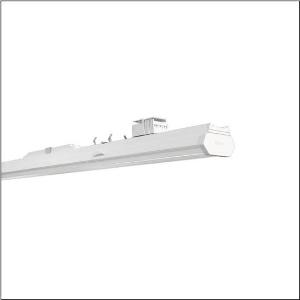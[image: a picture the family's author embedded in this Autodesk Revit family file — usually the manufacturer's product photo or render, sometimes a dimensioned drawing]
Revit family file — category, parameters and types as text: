
# Revit family: licross_r__21_protected_ho_52td12dn4e5m3c_ce33
name_source: partatom
category: Lighting Fixtures
units: mm (PartAtom-declared; Revit-internal decimal feet)

## family parameters
Cut with Voids When Loaded = No
Host = Face
Light Source = No
Part Type = Normal
Room Calculation Point = No
Round Connector Dimension = Use Diameter
Shared = No

## types (1)
- --- (1 x LED, 910 lm, 7.6 W, 4000K)
    Apparent Load = 8 VA
    CIE Flux Codes = 70 91 97 98 100
    Color Rendering = 80
    Color Temperature = 4000K
    Default Elevation = 1800 mm
    Description = Licross® 21 Protected HO, luminaire insert, of sheet steel, galvanised, coil coated, white, length: 1.500mm, width: 90mm, height: 103mm, LED rated luminous flux: 14.690lm, light colour: 840, SDCM (Standard Deviation of Colour Matching)MacAdam ≤ 3 SDCM (initial), control gear: DALI 2 (for two DALI lines), with plug, 6-pole, with phase selection, for trunking rail, 14-core, mains connection: 220..240V, AC, 50/60Hz, rated input power: 89W, for trunking rail, 14-core, internal wiring halogen-free, for emergency light function, converter,control gear: single battery element, battery: LiFePO4, 9Ah, primary light control with lens, of plastic, primary optical cover: cover, of PMMA, light emission: direct distribution, primary light characteristic: symmetric, protection rating (complete): IP54, insulation class (complete): insulation class I (protective earthing), certification: CE, UKCA, protection symbol: D if used in an environment with non-conductive dust loads with corresponding accessories, impact resistance: IK06, permissible ambient temperature for indoor applications: +5..+30°C, standard: EN 60598-2-22, LABS conformity tested according to VDMA 24364:2018-05, reducing of maximum allowable ambient temperature of 5°C with ceiling mounting, corresponds to IFS (International Featured Standards) requirements for safety and quality in the food industry, packaging unit: 1 piece
    Height = 92 mm
    Lamp = 1 x LED
    Lamp Light Flux = 910 lm
    Lamp Power = 7.6 W
    Lamp count = 1
    Length = 1500 mm
    Luminous efficacy = 120 lm/W
    Manufacturer = Siteco
    ModVariant = No
    Model = 52TD12DN4E5M3C
    Mounting Place = Ceiling
    Mounting Type = Pendant
    Number of Poles = 1
    OnlyDefault = Yes
    Power Factor = 1
    Product Name = Licross® 21 Protected HO
    Product group = luminaire insert | ceiling pendant
    ProductGroupID = 901
    Protection Class = Protection class I
    Protection Degree = IP 54
    RLX_Detail_Level = 1
    RLX_Emergency_Light_Flux = 0 lm
    RLX_Emergency_Type = 0
    RLX_Emergency_Type_DB = No
    RlxData = <blob elided: 25121 chars, md5=80ba49ea>
    Socket = socket
    Standby Power = 0 W
    System Light Flux = 910 lm
    System Power = 8 W
    Type Comments = : emergency light operation: 3 h
    Type Image = l_1256148.jpg
    URL = http://relux.com
    VarID = @adj_115133
    Voltage = 0 V
    Weight = 0.00 kg
    Width = 88 mm

## geometry (parser evidence)
native form markers: Blend x4, Sweep x11
no freeform markers — native parametric forms only
